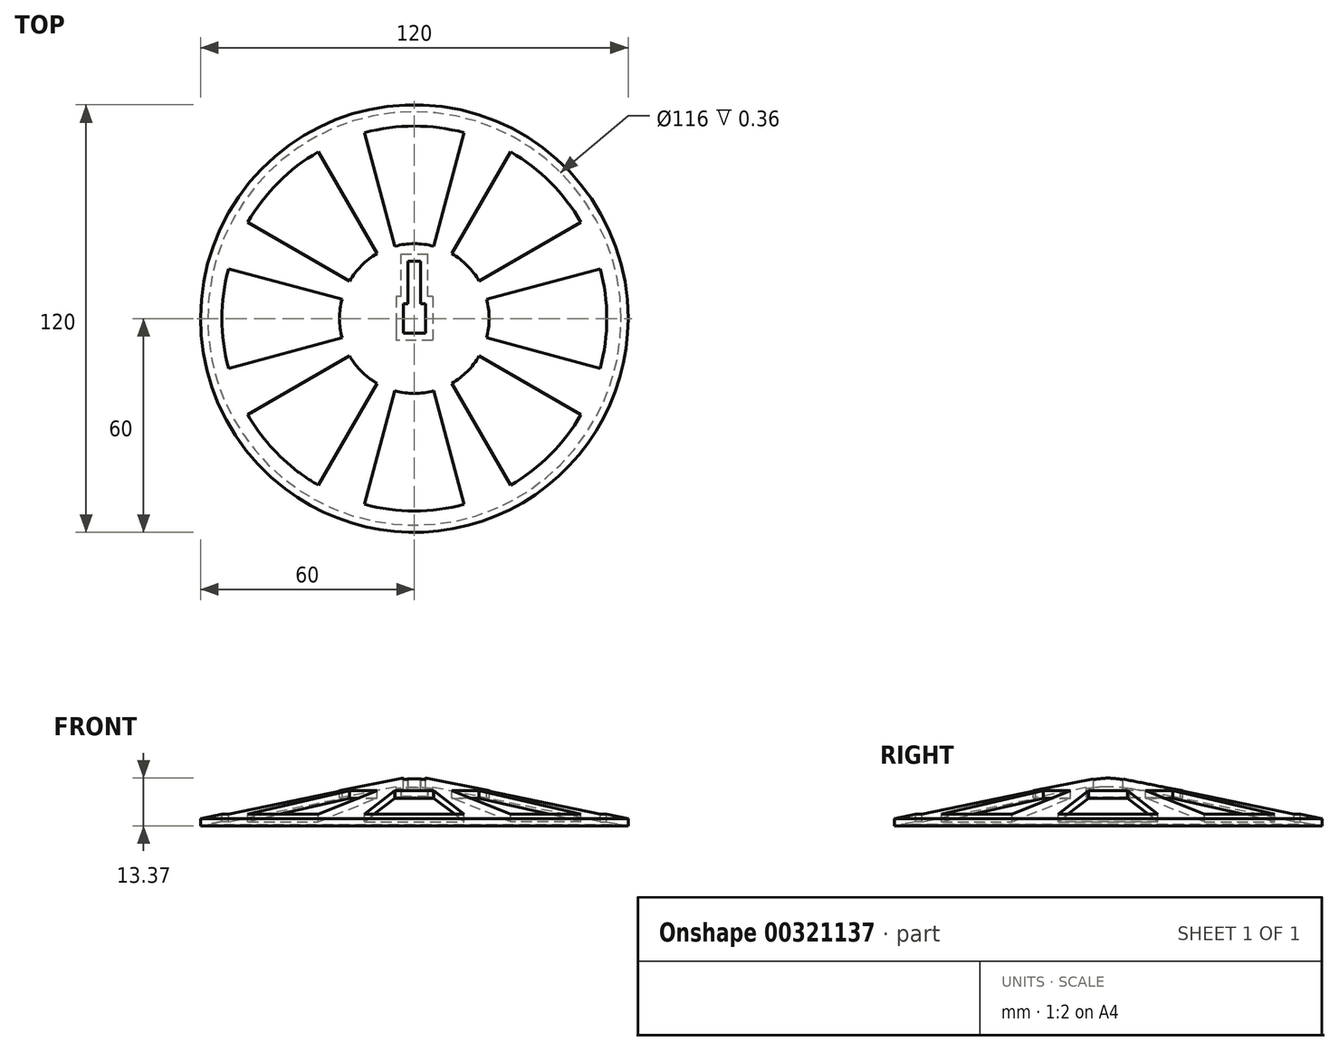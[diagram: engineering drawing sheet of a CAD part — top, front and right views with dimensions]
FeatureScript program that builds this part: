
annotation { "Feature Type Name" : "Feature", "Feature Type Description" : "" }
export const myFeature = defineFeature(function(context is Context, id is Id, definition is map)
    precondition{}
    {
        {
            var Q0;
            Q0=qCreatedBy(makeId("Front.planeOp"),FACE);
            var sketch = newSketch(context, id + "F0", { "sketchPlane" : qUnion([Q0])});
            skLineSegment(sketch, "E0", {"start": v(0, 14) * mm, "end": v(60, 2) * mm});
            skLineSegment(sketch, "E1", {"start": v(60, 2) * mm, "end": v(60, 0) * mm});
            skLineSegment(sketch, "E2", {"start": v(60, 0) * mm, "end": v(0, 0) * mm});
            skLineSegment(sketch, "E3", {"start": v(0, 14) * mm, "end": v(0, 0) * mm});
            skSolve(sketch);
        }
        {
            var Q0;
            Q0=makeQuery(id+"F0.imprint","IMPRINT",FACE,{"disambiguationData":[TD([[makeQuery(id+"F0.imprint","IMPRINT",EDGE,{"derivedFrom":sQuery(id+"F0.wireOp",EDGE,"E0")}),-1.0]])]});
            var Q1;
            Q1=sQuery(id+"F0.wireOp",EDGE,"E3");
            revolve(context, id + "F1", {"entities" : qUnion([Q0]), "axis" : qUnion([Q1]), "revolveType" : RevolveType.FULL});
        }
        {
            var Q0;
            Q0=qCreatedBy(makeId("Top.planeOp"),FACE);
            cPlane(context, id + "F2", {"entities" : qUnion([Q0]), "cplaneType" : CPlaneType.OFFSET, "offset" : 14 * mm, "width" : 152.4 * mm, "height" : 152.4 * mm});
        }
        {
            var Q0;
            Q0=qCreatedBy(id+"F2.planeOp",FACE);
            var sketch = newSketch(context, id + "F3", { "sketchPlane" : qUnion([Q0])});
            skLineSegment(sketch, "E4.bottom", {"start": v(3.12, 4.12) * mm, "end": v(-3.13, 4.12) * mm});
            skLineSegment(sketch, "E4.top", {"start": v(3.13, -4.12) * mm, "end": v(-3.12, -4.12) * mm});
            skLineSegment(sketch, "E4.left", {"start": v(3.12, 4.12) * mm, "end": v(3.13, -4.12) * mm});
            skLineSegment(sketch, "E4.right", {"start": v(-3.13, 4.12) * mm, "end": v(-3.12, -4.12) * mm});
            skPoint(sketch, "E4.middle", {"position": v(0, 0) * mm});
            skLineSegment(sketch, "E5.bottom", {"start": v(-1.75, 4.12) * mm, "end": v(1.75, 4.12) * mm});
            skLineSegment(sketch, "E5.top", {"start": v(-1.75, 16.12) * mm, "end": v(1.75, 16.12) * mm});
            skLineSegment(sketch, "E5.left", {"start": v(-1.75, 4.12) * mm, "end": v(-1.75, 16.12) * mm});
            skLineSegment(sketch, "E5.right", {"start": v(1.75, 4.12) * mm, "end": v(1.75, 16.12) * mm});
            skPoint(sketch, "E5.middle", {"position": v(0, 10.12) * mm});
            skSolve(sketch);
        }
        {
            var Q0;
            Q0 = qSketchRegion(id + "F3", true);
            extrude(context, id + "F4", {"entities" : qUnion([Q0]), "operationType" : NewBodyOperationType.REMOVE, "oppositeDirection" : true, "depth" : 4 * mm});
        }
        {
            var Q0;
            Q0=makeQuery(id+"F1.opRevolve","SWEPT_FACE",FACE,{"disambiguationData":[OSD([sQuery(id+"F0.wireOp",EDGE,"E2")])]});
            shell(context, id + "F5", {"entities" : qUnion([Q0]), "thickness" : 2 * mm});
        }
        {
            var Q0;
            Q0=qCreatedBy(id+"F2.planeOp",FACE);
            var sketch = newSketch(context, id + "F6", { "sketchPlane" : qUnion([Q0])});
            skArc(sketch, "E6", {"start": v(-5.44, -20.28) * mm, "mid": v(0, -21) * mm, "end": v(5.44, -20.28) * mm});
            skArc(sketch, "E7", {"start": v(-13.98, -52.16) * mm, "mid": v(0, -54) * mm, "end": v(13.98, -52.16) * mm});
            skLineSegment(sketch, "E8", {"start": v(-5.44, -20.28) * mm, "end": v(-13.98, -52.16) * mm});
            skLineSegment(sketch, "E9", {"start": v(5.44, -20.28) * mm, "end": v(13.98, -52.16) * mm});
            skLineSegment(sketch, "E10", {"start": v(0, 0) * mm, "end": v(0, -54) * mm, "construction": true});
            skArc(sketch, "E11.1.0", {"start": v(10.5, -18.19) * mm, "mid": v(14.85, -14.85) * mm, "end": v(18.19, -10.5) * mm});
            skLineSegment(sketch, "E11.1.1", {"start": v(10.5, -18.19) * mm, "end": v(27, -46.77) * mm});
            skLineSegment(sketch, "E11.1.2", {"start": v(18.19, -10.5) * mm, "end": v(46.77, -27) * mm});
            skArc(sketch, "E11.1.3", {"start": v(27, -46.77) * mm, "mid": v(38.18, -38.18) * mm, "end": v(46.77, -27) * mm});
            skArc(sketch, "E11.2.0", {"start": v(20.28, -5.44) * mm, "mid": v(21, 0) * mm, "end": v(20.28, 5.44) * mm});
            skLineSegment(sketch, "E11.2.1", {"start": v(20.28, -5.44) * mm, "end": v(52.16, -13.98) * mm});
            skLineSegment(sketch, "E11.2.2", {"start": v(20.28, 5.44) * mm, "end": v(52.16, 13.98) * mm});
            skArc(sketch, "E11.2.3", {"start": v(52.16, -13.98) * mm, "mid": v(54, 0) * mm, "end": v(52.16, 13.98) * mm});
            skArc(sketch, "E11.3.0", {"start": v(18.19, 10.5) * mm, "mid": v(14.85, 14.85) * mm, "end": v(10.5, 18.19) * mm});
            skLineSegment(sketch, "E11.3.1", {"start": v(18.19, 10.5) * mm, "end": v(46.77, 27) * mm});
            skLineSegment(sketch, "E11.3.2", {"start": v(10.5, 18.19) * mm, "end": v(27, 46.77) * mm});
            skArc(sketch, "E11.3.3", {"start": v(46.77, 27) * mm, "mid": v(38.18, 38.18) * mm, "end": v(27, 46.77) * mm});
            skArc(sketch, "E11.4.0", {"start": v(5.44, 20.28) * mm, "mid": v(0, 21) * mm, "end": v(-5.44, 20.28) * mm});
            skLineSegment(sketch, "E11.4.1", {"start": v(5.44, 20.28) * mm, "end": v(13.98, 52.16) * mm});
            skLineSegment(sketch, "E11.4.2", {"start": v(-5.44, 20.28) * mm, "end": v(-13.98, 52.16) * mm});
            skArc(sketch, "E11.4.3", {"start": v(13.98, 52.16) * mm, "mid": v(0, 54) * mm, "end": v(-13.98, 52.16) * mm});
            skArc(sketch, "E11.5.0", {"start": v(-10.5, 18.19) * mm, "mid": v(-14.85, 14.85) * mm, "end": v(-18.19, 10.5) * mm});
            skLineSegment(sketch, "E11.5.1", {"start": v(-10.5, 18.19) * mm, "end": v(-27, 46.77) * mm});
            skLineSegment(sketch, "E11.5.2", {"start": v(-18.19, 10.5) * mm, "end": v(-46.77, 27) * mm});
            skArc(sketch, "E11.5.3", {"start": v(-27, 46.77) * mm, "mid": v(-38.18, 38.18) * mm, "end": v(-46.77, 27) * mm});
            skArc(sketch, "E11.6.0", {"start": v(-20.28, 5.44) * mm, "mid": v(-21, 0) * mm, "end": v(-20.28, -5.44) * mm});
            skLineSegment(sketch, "E11.6.1", {"start": v(-20.28, 5.44) * mm, "end": v(-52.16, 13.98) * mm});
            skLineSegment(sketch, "E11.6.2", {"start": v(-20.28, -5.44) * mm, "end": v(-52.16, -13.98) * mm});
            skArc(sketch, "E11.6.3", {"start": v(-52.16, 13.98) * mm, "mid": v(-54, 0) * mm, "end": v(-52.16, -13.98) * mm});
            skArc(sketch, "E11.7.0", {"start": v(-18.19, -10.5) * mm, "mid": v(-14.85, -14.85) * mm, "end": v(-10.5, -18.19) * mm});
            skLineSegment(sketch, "E11.7.1", {"start": v(-18.19, -10.5) * mm, "end": v(-46.77, -27) * mm});
            skLineSegment(sketch, "E11.7.2", {"start": v(-10.5, -18.19) * mm, "end": v(-27, -46.77) * mm});
            skArc(sketch, "E11.7.3", {"start": v(-46.77, -27) * mm, "mid": v(-38.18, -38.18) * mm, "end": v(-27, -46.77) * mm});
            skSolve(sketch);
        }
        {
            var Q0;
            Q0=makeQuery(id+"F6.imprint","IMPRINT",FACE,{"disambiguationData":[TD([[makeQuery(id+"F6.imprint","IMPRINT",EDGE,{"derivedFrom":sQuery(id+"F6.wireOp",EDGE,"E6")}),-1.0]])]});
            var Q1;
            Q1=makeQuery(id+"F6.imprint","IMPRINT",FACE,{"disambiguationData":[TD([[makeQuery(id+"F6.imprint","IMPRINT",EDGE,{"derivedFrom":sQuery(id+"F6.wireOp",EDGE,"E11.1.0")}),-1.0]])]});
            var Q2;
            Q2=makeQuery(id+"F6.imprint","IMPRINT",FACE,{"disambiguationData":[TD([[makeQuery(id+"F6.imprint","IMPRINT",EDGE,{"derivedFrom":sQuery(id+"F6.wireOp",EDGE,"E11.2.0")}),-1.0]])]});
            var Q3;
            Q3=makeQuery(id+"F6.imprint","IMPRINT",FACE,{"disambiguationData":[TD([[makeQuery(id+"F6.imprint","IMPRINT",EDGE,{"derivedFrom":sQuery(id+"F6.wireOp",EDGE,"E11.3.0")}),-1.0]])]});
            var Q4;
            Q4=makeQuery(id+"F6.imprint","IMPRINT",FACE,{"disambiguationData":[TD([[makeQuery(id+"F6.imprint","IMPRINT",EDGE,{"derivedFrom":sQuery(id+"F6.wireOp",EDGE,"E11.4.0")}),-1.0]])]});
            var Q5;
            Q5=makeQuery(id+"F6.imprint","IMPRINT",FACE,{"disambiguationData":[TD([[makeQuery(id+"F6.imprint","IMPRINT",EDGE,{"derivedFrom":sQuery(id+"F6.wireOp",EDGE,"E11.5.0")}),-1.0]])]});
            var Q6;
            Q6=makeQuery(id+"F6.imprint","IMPRINT",FACE,{"disambiguationData":[TD([[makeQuery(id+"F6.imprint","IMPRINT",EDGE,{"derivedFrom":sQuery(id+"F6.wireOp",EDGE,"E11.6.0")}),-1.0]])]});
            var Q7;
            Q7=makeQuery(id+"F6.imprint","IMPRINT",FACE,{"disambiguationData":[TD([[makeQuery(id+"F6.imprint","IMPRINT",EDGE,{"derivedFrom":sQuery(id+"F6.wireOp",EDGE,"E11.7.0")}),-1.0]])]});
            extrude(context, id + "F7", {"entities" : qUnion([Q0, Q1, Q2, Q3, Q4, Q5, Q6, Q7]), "operationType" : NewBodyOperationType.REMOVE, "oppositeDirection" : true, "depth" : 25 * mm});
        }
    });
